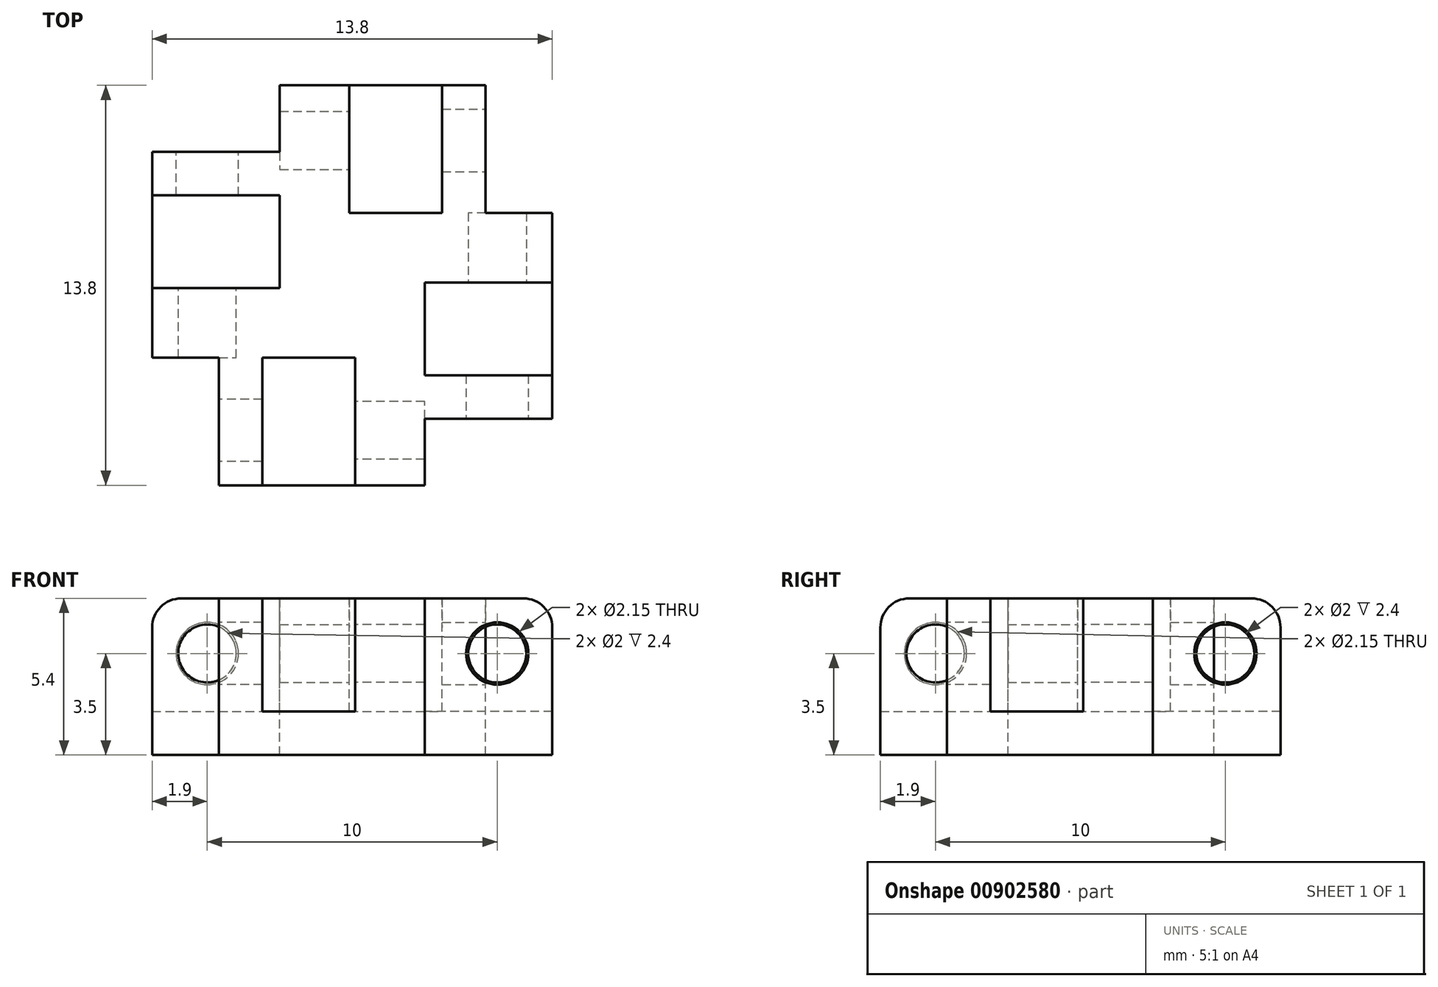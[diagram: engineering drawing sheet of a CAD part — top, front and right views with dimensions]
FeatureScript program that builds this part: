
annotation { "Feature Type Name" : "Feature", "Feature Type Description" : "" }
export const myFeature = defineFeature(function(context is Context, id is Id, definition is map)
    precondition{}
    {
        {
            var Q0;
            Q0=qCreatedBy(makeId("Top.planeOp"),FACE);
            var sketch = newSketch(context, id + "F0", { "sketchPlane" : qUnion([Q0])});
            skLineSegment(sketch, "E0.bottom", {"start": v(6.5, -6.5) * mm, "end": v(-6.5, -6.5) * mm});
            skLineSegment(sketch, "E0.top", {"start": v(6.5, 6.5) * mm, "end": v(-6.5, 6.5) * mm});
            skLineSegment(sketch, "E0.left", {"start": v(6.5, -6.5) * mm, "end": v(6.5, 6.5) * mm});
            skLineSegment(sketch, "E0.right", {"start": v(-6.5, -6.5) * mm, "end": v(-6.5, 6.5) * mm});
            skPoint(sketch, "E0.middle", {"position": v(0, 0) * mm});
            skSolve(sketch);
        }
        {
            var Q0;
            Q0=makeQuery(id+"F0.imprint","IMPRINT",FACE,{"disambiguationData":[TD([[makeQuery(id+"F0.imprint","IMPRINT",EDGE,{"derivedFrom":sQuery(id+"F0.wireOp",EDGE,"E0.bottom")}),-1.0]])]});
            extrude(context, id + "F1", {"entities" : qUnion([Q0]), "depth" : 5 * mm, "offsetDistance" : 25 * mm});
        }
        {
            var Q0;
            Q0=makeQuery(id+"F1.opExtrude","CAP_FACE",FACE,{"disambiguationData":[OSD([sQuery(id+"F0.wireOp",EDGE,"E0.bottom"),sQuery(id+"F0.wireOp",EDGE,"E0.top"),sQuery(id+"F0.wireOp",EDGE,"E0.left"),sQuery(id+"F0.wireOp",EDGE,"E0.right")])],"isStart":false});
            var sketch = newSketch(context, id + "F2", { "sketchPlane" : qUnion([Q0])});
            skLineSegment(sketch, "E1.bottom", {"start": v(-0.1, 6.5) * mm, "end": v(3.1, 6.5) * mm});
            skLineSegment(sketch, "E1.top", {"start": v(-0.1, 2.5) * mm, "end": v(3.1, 2.5) * mm});
            skLineSegment(sketch, "E1.left", {"start": v(-0.1, 6.5) * mm, "end": v(-0.1, 2.5) * mm});
            skLineSegment(sketch, "E1.right", {"start": v(3.1, 6.5) * mm, "end": v(3.1, 2.5) * mm});
            skPoint(sketch, "E2", {"position": v(1.5, 2.5) * mm});
            skLineSegment(sketch, "E3.1.0", {"start": v(-6.5, 3.1) * mm, "end": v(-2.5, 3.1) * mm});
            skLineSegment(sketch, "E3.1.1", {"start": v(-6.5, -0.1) * mm, "end": v(-6.5, 3.1) * mm});
            skLineSegment(sketch, "E3.1.2", {"start": v(-6.5, -0.1) * mm, "end": v(-2.5, -0.1) * mm});
            skLineSegment(sketch, "E3.1.3", {"start": v(-2.5, -0.1) * mm, "end": v(-2.5, 3.1) * mm});
            skLineSegment(sketch, "E3.2.0", {"start": v(-3.1, -6.5) * mm, "end": v(-3.1, -2.5) * mm});
            skLineSegment(sketch, "E3.2.1", {"start": v(0.1, -6.5) * mm, "end": v(-3.1, -6.5) * mm});
            skLineSegment(sketch, "E3.2.2", {"start": v(0.1, -6.5) * mm, "end": v(0.1, -2.5) * mm});
            skLineSegment(sketch, "E3.2.3", {"start": v(0.1, -2.5) * mm, "end": v(-3.1, -2.5) * mm});
            skLineSegment(sketch, "E3.3.0", {"start": v(6.5, -3.1) * mm, "end": v(2.5, -3.1) * mm});
            skLineSegment(sketch, "E3.3.1", {"start": v(6.5, 0.1) * mm, "end": v(6.5, -3.1) * mm});
            skLineSegment(sketch, "E3.3.2", {"start": v(6.5, 0.1) * mm, "end": v(2.5, 0.1) * mm});
            skLineSegment(sketch, "E3.3.3", {"start": v(2.5, 0.1) * mm, "end": v(2.5, -3.1) * mm});
            skPoint(sketch, "E3.center", {"position": v(0, 0) * mm});
            skSolve(sketch);
        }
        {
            var Q0;
            Q0 = qSketchRegion(id + "F2", true);
            extrude(context, id + "F3", {"entities" : qUnion([Q0]), "operationType" : NewBodyOperationType.REMOVE, "oppositeDirection" : true, "depth" : 3.5 * mm, "offsetDistance" : 25 * mm});
        }
        {
            var Q0;
            Q0=makeQuery(id+"F1.opExtrude","CAP_FACE",FACE,{"disambiguationData":[OSD([sQuery(id+"F0.wireOp",EDGE,"E0.bottom"),sQuery(id+"F0.wireOp",EDGE,"E0.top"),sQuery(id+"F0.wireOp",EDGE,"E0.left"),sQuery(id+"F0.wireOp",EDGE,"E0.right")])],"isStart":false});
            var sketch = newSketch(context, id + "F4", { "sketchPlane" : qUnion([Q0])});
            skLineSegment(sketch, "E4.bottom", {"start": v(-6.5, 6.5) * mm, "end": v(-2.5, 6.5) * mm});
            skLineSegment(sketch, "E4.top", {"start": v(-6.5, 4.6) * mm, "end": v(-2.5, 4.6) * mm});
            skLineSegment(sketch, "E4.left", {"start": v(-6.5, 6.5) * mm, "end": v(-6.5, 4.6) * mm});
            skLineSegment(sketch, "E4.right", {"start": v(-2.5, 6.5) * mm, "end": v(-2.5, 4.6) * mm});
            skLineSegment(sketch, "E5.1.0", {"start": v(-6.5, -6.5) * mm, "end": v(-6.5, -2.5) * mm});
            skLineSegment(sketch, "E5.1.1", {"start": v(-6.5, -6.5) * mm, "end": v(-4.6, -6.5) * mm});
            skLineSegment(sketch, "E5.1.2", {"start": v(-6.5, -2.5) * mm, "end": v(-4.6, -2.5) * mm});
            skLineSegment(sketch, "E5.1.3", {"start": v(-4.6, -6.5) * mm, "end": v(-4.6, -2.5) * mm});
            skLineSegment(sketch, "E5.2.0", {"start": v(6.5, -6.5) * mm, "end": v(2.5, -6.5) * mm});
            skLineSegment(sketch, "E5.2.1", {"start": v(6.5, -6.5) * mm, "end": v(6.5, -4.6) * mm});
            skLineSegment(sketch, "E5.2.2", {"start": v(2.5, -6.5) * mm, "end": v(2.5, -4.6) * mm});
            skLineSegment(sketch, "E5.2.3", {"start": v(6.5, -4.6) * mm, "end": v(2.5, -4.6) * mm});
            skLineSegment(sketch, "E5.3.0", {"start": v(6.5, 6.5) * mm, "end": v(6.5, 2.5) * mm});
            skLineSegment(sketch, "E5.3.1", {"start": v(6.5, 6.5) * mm, "end": v(4.6, 6.5) * mm});
            skLineSegment(sketch, "E5.3.2", {"start": v(6.5, 2.5) * mm, "end": v(4.6, 2.5) * mm});
            skLineSegment(sketch, "E5.3.3", {"start": v(4.6, 6.5) * mm, "end": v(4.6, 2.5) * mm});
            skPoint(sketch, "E5.center", {"position": v(0, 0) * mm});
            skSolve(sketch);
        }
        {
            var Q0;
            Q0 = qSketchRegion(id + "F4", true);
            var Q1;
            Q1=makeQuery(id+"F1.opExtrude","CAP_FACE",FACE,{"disambiguationData":[OSD([sQuery(id+"F0.wireOp",EDGE,"E0.bottom"),sQuery(id+"F0.wireOp",EDGE,"E0.top"),sQuery(id+"F0.wireOp",EDGE,"E0.left"),sQuery(id+"F0.wireOp",EDGE,"E0.right")])],"isStart":true});
            extrude(context, id + "F5", {"entities" : qUnion([Q0]), "operationType" : NewBodyOperationType.REMOVE, "endBound" : BoundingType.UP_TO_SURFACE, "oppositeDirection" : true, "depth" : 25 * mm, "endBoundEntityFace" : qUnion([Q1]), "offsetDistance" : 25 * mm});
        }
        {
            var Q0;
            Q0=qCreatedBy(makeId("Top.planeOp"),FACE);
            var sketch = newSketch(context, id + "F6", { "sketchPlane" : qUnion([Q0])});
            skLineSegment(sketch, "E6.bottom", {"start": v(0, 0) * mm, "end": v(-6.5, 0) * mm});
            skLineSegment(sketch, "E6.top", {"start": v(0, 6.5) * mm, "end": v(-6.5, 6.5) * mm});
            skLineSegment(sketch, "E6.left", {"start": v(0, 0) * mm, "end": v(0, 6.5) * mm});
            skLineSegment(sketch, "E6.right", {"start": v(-6.5, 0) * mm, "end": v(-6.5, 6.5) * mm});
            skSolve(sketch);
        }
        {
            var Q0;
            Q0=makeQuery(id+"F6.imprint","IMPRINT",FACE,{"disambiguationData":[TD([[makeQuery(id+"F6.imprint","IMPRINT",EDGE,{"derivedFrom":sQuery(id+"F6.wireOp",EDGE,"E6.bottom")}),-1.0]])]});
            var Q1;
            Q1=makeQuery(id+"F1.opExtrude","CAP_FACE",FACE,{"disambiguationData":[OSD([sQuery(id+"F0.wireOp",EDGE,"E0.bottom"),sQuery(id+"F0.wireOp",EDGE,"E0.top"),sQuery(id+"F0.wireOp",EDGE,"E0.left"),sQuery(id+"F0.wireOp",EDGE,"E0.right")])],"isStart":false});
            extrude(context, id + "F7", {"entities" : qUnion([Q0]), "operationType" : NewBodyOperationType.INTERSECT, "endBound" : BoundingType.UP_TO_SURFACE, "depth" : 25 * mm, "endBoundEntityFace" : qUnion([Q1]), "offsetDistance" : 25 * mm});
        }
        {
            var Q0;
            Q0=makeQuery(id+"F5.boolean.opBoolean","COPY",FACE,{"derivedFrom":makeQuery(id+"F5.opExtrude","SWEPT_FACE",FACE,{"disambiguationData":[OSD([sQuery(id+"F4.wireOp",EDGE,"E4.top")])]})});
            var sketch = newSketch(context, id + "F8", { "sketchPlane" : qUnion([Q0])});
            skCircle(sketch, "E7", {"center": v(5, 3.5) * mm, "radius": 1.07 * mm});
            skLineSegment(sketch, "E8", {"start": v(5, 3.5) * mm, "end": v(5, 5) * mm, "construction": true});
            skLineSegment(sketch, "E9", {"start": v(5, 3.5) * mm, "end": v(6.5, 3.5) * mm, "construction": true});
            skSolve(sketch);
        }
        {
            var Q0;
            Q0=makeQuery(id+"F7.boolean.opBoolean","MERGE",FACE,{"derivedFrom":[makeQuery(id+"F3.boolean.opBoolean","COPY",FACE,{"derivedFrom":makeQuery(id+"F3.opExtrude","SWEPT_FACE",FACE,{"disambiguationData":[OSD([sQuery(id+"F2.wireOp",EDGE,"E1.left")])]})})],"fromTools":[makeQuery(id+"F7.boolean.toolComplement.opBoolean","COPY",FACE,{"derivedFrom":makeQuery(id+"F7.opExtrude","SWEPT_FACE",FACE,{"disambiguationData":[OSD([sQuery(id+"F6.wireOp",EDGE,"E6.left")])]})})]});
            var sketch = newSketch(context, id + "F9", { "sketchPlane" : qUnion([Q0])});
            skCircle(sketch, "E10", {"center": v(5, 3.5) * mm, "radius": 1 * mm});
            skLineSegment(sketch, "E11", {"start": v(5, 5) * mm, "end": v(5, 3.5) * mm, "construction": true});
            skLineSegment(sketch, "E12", {"start": v(5, 3.5) * mm, "end": v(6.5, 3.5) * mm, "construction": true});
            skSolve(sketch);
        }
        {
            var Q0;
            Q0=makeQuery(id+"F1.opExtrude","CAP_FACE",FACE,{"disambiguationData":[OSD([sQuery(id+"F0.wireOp",EDGE,"E0.bottom"),sQuery(id+"F0.wireOp",EDGE,"E0.top"),sQuery(id+"F0.wireOp",EDGE,"E0.left"),sQuery(id+"F0.wireOp",EDGE,"E0.right")])],"isStart":false});
            extrude(context, id + "F10", {"entities" : qUnion([Q0]), "operationType" : NewBodyOperationType.ADD, "depth" : 0.4 * mm, "offsetDistance" : 25 * mm});
        }
        {
            var Q0;
            {var subQ0=sQuery(id+"F0.wireOp",EDGE,"E0.right");Q0=makeQuery(id+"F10.boolean.opBoolean","MERGE",FACE,{"derivedFrom":[makeQuery(id+"F1.opExtrude","SWEPT_FACE",FACE,{"disambiguationData":[OSD([subQ0])]}),makeQuery(id+"F10.opExtrude","SWEPT_FACE",FACE,{"disambiguationData":[OSD([subQ0])]})]});}
            extrude(context, id + "F11", {"entities" : qUnion([Q0]), "operationType" : NewBodyOperationType.ADD, "depth" : 0.4 * mm, "offsetDistance" : 25 * mm});
        }
        {
            var Q0;
            {var subQ0=sQuery(id+"F0.wireOp",EDGE,"E0.top");Q0=makeQuery(id+"F10.boolean.opBoolean","MERGE",FACE,{"derivedFrom":[makeQuery(id+"F1.opExtrude","SWEPT_FACE",FACE,{"disambiguationData":[OSD([subQ0])]}),makeQuery(id+"F10.opExtrude","SWEPT_FACE",FACE,{"disambiguationData":[OSD([subQ0])]})]});}
            extrude(context, id + "F12", {"entities" : qUnion([Q0]), "operationType" : NewBodyOperationType.ADD, "depth" : 0.4 * mm, "offsetDistance" : 25 * mm});
        }
        {
            var Q0;
            Q0=makeQuery(id+"F8.imprint","IMPRINT",FACE,{"disambiguationData":[TD([[makeQuery(id+"F8.imprint","IMPRINT",EDGE,{"derivedFrom":sQuery(id+"F8.wireOp",EDGE,"E7")}),1.0]])]});
            var Q1;
            Q1=sQuery(id+"F8.wireOp",EDGE,"E7");
            var Q2;
            {var subQ0=sQuery(id+"F2.wireOp",EDGE,"E3.1.0");Q2=makeQuery(id+"F11.boolean.opBoolean","MERGE",FACE,{"derivedFrom":[makeQuery(id+"F10.boolean.opBoolean","MERGE",FACE,{"derivedFrom":[makeQuery(id+"F3.boolean.opBoolean","COPY",FACE,{"derivedFrom":makeQuery(id+"F3.opExtrude","SWEPT_FACE",FACE,{"disambiguationData":[OSD([subQ0])]})}),makeQuery(id+"F10.opExtrude","SWEPT_FACE",FACE,{"disambiguationData":[OSD([subQ0])]})]}),makeQuery(id+"F11.opExtrude","SWEPT_FACE",FACE,{"disambiguationData":[OSD([sQuery(id+"F0.wireOp",EDGE,"E0.right"),subQ0,sQuery(id+"F2.wireOp",EDGE,"E3.1.1")])]})]});}
            extrude(context, id + "F13", {"entities" : qUnion([Q0]), "operationType" : NewBodyOperationType.REMOVE, "surfaceEntities" : qUnion([Q1]), "endBound" : BoundingType.UP_TO_SURFACE, "oppositeDirection" : true, "depth" : 25 * mm, "endBoundEntityFace" : qUnion([Q2]), "offsetDistance" : 25 * mm});
        }
        {
            var Q0;
            Q0=makeQuery(id+"F9.imprint","IMPRINT",FACE,{"disambiguationData":[TD([[makeQuery(id+"F9.imprint","IMPRINT",EDGE,{"derivedFrom":sQuery(id+"F9.wireOp",EDGE,"E10")}),1.0]])]});
            var Q1;
            {var subQ0=sQuery(id+"F4.wireOp",EDGE,"E4.right");Q1=makeQuery(id+"F10.boolean.opBoolean","MERGE",FACE,{"derivedFrom":[makeQuery(id+"F5.boolean.opBoolean","COPY",FACE,{"derivedFrom":makeQuery(id+"F5.opExtrude","SWEPT_FACE",FACE,{"disambiguationData":[OSD([subQ0])]})}),makeQuery(id+"F10.opExtrude","SWEPT_FACE",FACE,{"disambiguationData":[OSD([subQ0])]})]});}
            extrude(context, id + "F14", {"entities" : qUnion([Q0]), "operationType" : NewBodyOperationType.REMOVE, "endBound" : BoundingType.UP_TO_SURFACE, "oppositeDirection" : true, "depth" : 2.5 * mm, "endBoundEntityFace" : qUnion([Q1]), "offsetDistance" : 25 * mm});
        }
        {
            var Q0;
            Q0=makeQuery(id+"F1.opExtrude","SWEPT_BODY",BODY,{"disambiguationData":[OSD([sQuery(id+"F0.wireOp",EDGE,"E0.bottom"),sQuery(id+"F0.wireOp",EDGE,"E0.top"),sQuery(id+"F0.wireOp",EDGE,"E0.left"),sQuery(id+"F0.wireOp",EDGE,"E0.right")])]});
            var Q1;
            {var subQ0=sQuery(id+"F6.wireOp",EDGE,"E6.left");var subQ1=sQuery(id+"F6.wireOp",EDGE,"E6.bottom");Q1=makeQuery(id+"F10.boolean.opBoolean","MERGE",EDGE,{"derivedFrom":[makeQuery(id+"F7.boolean.opBoolean","COPY",EDGE,{"derivedFrom":makeQuery(id+"F7.boolean.toolComplement.opBoolean","COPY",EDGE,{"derivedFrom":makeQuery(id+"F7.opExtrude","SWEPT_EDGE",EDGE,{"disambiguationData":[OSD([subQ1,subQ0])]})})}),makeQuery(id+"F10.opExtrude","SWEPT_EDGE",EDGE,{"disambiguationData":[OSD([subQ1,subQ0])]})]});}
            circularPattern(context, id + "F15", {"operationType" : NewBodyOperationType.ADD, "entities" : qUnion([Q0]), "axis" : qUnion([Q1]), "angle" : 360 * degree, "instanceCount" : 4, "equalSpace" : true});
        }
        {
            var Q0;
            {var subQ0=sQuery(id+"F0.wireOp",EDGE,"E0.top");Q0=makeQuery(id+"F15.opPattern","COPY",EDGE,{"derivedFrom":makeQuery(id+"F12.opExtrude","CAP_EDGE",EDGE,{"disambiguationData":[OSD([subQ0]),TDD([makeQuery(id+"F10.opExtrude","CAP_EDGE",EDGE,{"disambiguationData":[OSD([subQ0])],"isStart":false})])],"isStart":false}),"instanceName":"3"});}
            var Q1;
            {var subQ0=sQuery(id+"F0.wireOp",EDGE,"E0.right");Q1=makeQuery(id+"F11.opExtrude","CAP_EDGE",EDGE,{"disambiguationData":[OSD([subQ0]),TDD([makeQuery(id+"F10.opExtrude","CAP_EDGE",EDGE,{"disambiguationData":[OSD([subQ0])],"isStart":false})])],"isStart":false});}
            var Q2;
            {var subQ0=sQuery(id+"F0.wireOp",EDGE,"E0.top");Q2=makeQuery(id+"F12.opExtrude","CAP_EDGE",EDGE,{"disambiguationData":[OSD([subQ0]),TDD([makeQuery(id+"F10.opExtrude","CAP_EDGE",EDGE,{"disambiguationData":[OSD([subQ0])],"isStart":false})])],"isStart":false});}
            var Q3;
            {var subQ0=sQuery(id+"F0.wireOp",EDGE,"E0.right");Q3=makeQuery(id+"F15.opPattern","COPY",EDGE,{"derivedFrom":makeQuery(id+"F11.opExtrude","CAP_EDGE",EDGE,{"disambiguationData":[OSD([subQ0]),TDD([makeQuery(id+"F10.opExtrude","CAP_EDGE",EDGE,{"disambiguationData":[OSD([subQ0])],"isStart":false})])],"isStart":false}),"instanceName":"1"});}
            var Q4;
            {var subQ0=sQuery(id+"F0.wireOp",EDGE,"E0.top");Q4=makeQuery(id+"F15.opPattern","COPY",EDGE,{"derivedFrom":makeQuery(id+"F12.opExtrude","CAP_EDGE",EDGE,{"disambiguationData":[OSD([subQ0]),TDD([makeQuery(id+"F10.opExtrude","CAP_EDGE",EDGE,{"disambiguationData":[OSD([subQ0])],"isStart":false})])],"isStart":false}),"instanceName":"1"});}
            var Q5;
            {var subQ0=sQuery(id+"F0.wireOp",EDGE,"E0.right");Q5=makeQuery(id+"F15.opPattern","COPY",EDGE,{"derivedFrom":makeQuery(id+"F11.opExtrude","CAP_EDGE",EDGE,{"disambiguationData":[OSD([subQ0]),TDD([makeQuery(id+"F10.opExtrude","CAP_EDGE",EDGE,{"disambiguationData":[OSD([subQ0])],"isStart":false})])],"isStart":false}),"instanceName":"2"});}
            var Q6;
            {var subQ0=sQuery(id+"F0.wireOp",EDGE,"E0.top");Q6=makeQuery(id+"F15.opPattern","COPY",EDGE,{"derivedFrom":makeQuery(id+"F12.opExtrude","CAP_EDGE",EDGE,{"disambiguationData":[OSD([subQ0]),TDD([makeQuery(id+"F10.opExtrude","CAP_EDGE",EDGE,{"disambiguationData":[OSD([subQ0])],"isStart":false})])],"isStart":false}),"instanceName":"2"});}
            var Q7;
            {var subQ0=sQuery(id+"F0.wireOp",EDGE,"E0.right");Q7=makeQuery(id+"F15.opPattern","COPY",EDGE,{"derivedFrom":makeQuery(id+"F11.opExtrude","CAP_EDGE",EDGE,{"disambiguationData":[OSD([subQ0]),TDD([makeQuery(id+"F10.opExtrude","CAP_EDGE",EDGE,{"disambiguationData":[OSD([subQ0])],"isStart":false})])],"isStart":false}),"instanceName":"3"});}
            fillet(context, id + "F16", {"entities" : qUnion([Q0, Q1, Q2, Q3, Q4, Q5, Q6, Q7]), "radius" : 1 * mm, "tangentPropagation" : true, "allowEdgeOverflow" : false});
        }
    });
